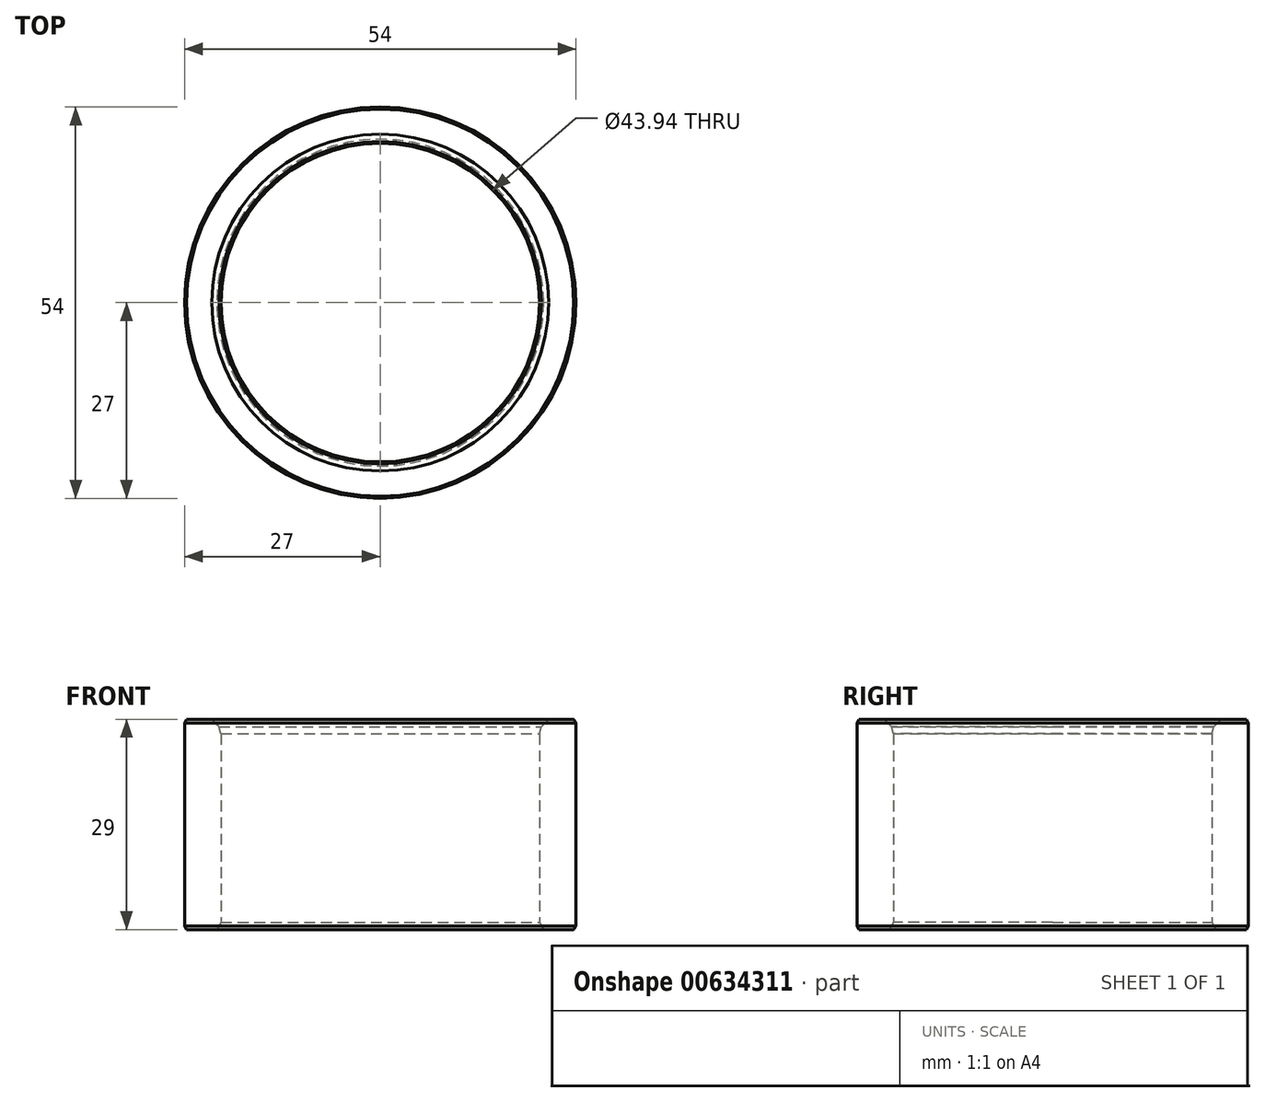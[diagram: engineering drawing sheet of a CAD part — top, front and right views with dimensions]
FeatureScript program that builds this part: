
annotation { "Feature Type Name" : "Feature", "Feature Type Description" : "" }
export const myFeature = defineFeature(function(context is Context, id is Id, definition is map)
    precondition{}
    {
        {
            var Q0;
            Q0=qCreatedBy(makeId("Top.planeOp"),FACE);
            var sketch = newSketch(context, id + "F0", { "sketchPlane" : qUnion([Q0])});
            skCircle(sketch, "E0", {"center": v(0, 0) * mm, "radius": 21.97 * mm});
            skCircle(sketch, "E1", {"center": v(0, 0) * mm, "radius": 27 * mm});
            skSolve(sketch);
        }
        {
            var Q0;
            Q0=makeQuery(id+"F0.imprint","IMPRINT",FACE,{"disambiguationData":[TD([[makeQuery(id+"F0.imprint","IMPRINT",EDGE,{"derivedFrom":sQuery(id+"F0.wireOp",EDGE,"E0")}),-1.0]])]});
            extrude(context, id + "F1", {"entities" : qUnion([Q0]), "depth" : 29 * mm, "offsetDistance" : 25 * mm});
        }
        {
            var Q0;
            Q0=makeQuery(id+"F1.opExtrude","CAP_EDGE",EDGE,{"disambiguationData":[OSD([sQuery(id+"F0.wireOp",EDGE,"E1")])],"isStart":false});
            var Q1;
            Q1=makeQuery(id+"F1.opExtrude","CAP_EDGE",EDGE,{"disambiguationData":[OSD([sQuery(id+"F0.wireOp",EDGE,"E1")])],"isStart":true});
            chamfer(context, id + "F2", {"entities" : qUnion([Q0, Q1]), "chamferType" : ChamferType.OFFSET_ANGLE, "width" : 0.5 * mm, "oppositeDirection" : true, "angle" : 30 * degree, "tangentPropagation" : true});
        }
        {
            var Q0;
            Q0=makeQuery(id+"F1.opExtrude","CAP_EDGE",EDGE,{"disambiguationData":[OSD([sQuery(id+"F0.wireOp",EDGE,"E0")])],"isStart":true});
            chamfer(context, id + "F3", {"entities" : qUnion([Q0]), "chamferType" : ChamferType.OFFSET_ANGLE, "width" : 1 * mm, "oppositeDirection" : true, "angle" : 30 * degree, "tangentPropagation" : true});
        }
        {
            var Q0;
            Q0=qCreatedBy(makeId("Front.planeOp"),FACE);
            var sketch = newSketch(context, id + "F4", { "sketchPlane" : qUnion([Q0])});
            skLineSegment(sketch, "E2", {"start": v(-21.97, 0) * mm, "end": v(-21.97, 29) * mm, "construction": true});
            skLineSegment(sketch, "E3", {"start": v(21.97, 29) * mm, "end": v(21.97, 0) * mm, "construction": true});
            skLineSegment(sketch, "E4.0.0", {"start": v(-26.71, 29) * mm, "end": v(26.71, 29) * mm, "construction": true});
            skLineSegment(sketch, "E5", {"start": v(-20.35, 28) * mm, "end": v(-23.75, 28) * mm, "construction": true});
            skLineSegment(sketch, "E6", {"start": v(-20.35, 27) * mm, "end": v(-23.75, 27) * mm, "construction": true});
            skLineSegment(sketch, "E7", {"start": v(-21.97, 27) * mm, "end": v(-22.24, 28) * mm});
            skLineSegment(sketch, "E8", {"start": v(-22.24, 28) * mm, "end": v(-23.24, 29) * mm});
            skLineSegment(sketch, "E9", {"start": v(-23.24, 29) * mm, "end": v(-21.97, 29) * mm});
            skLineSegment(sketch, "E10", {"start": v(-21.97, 27) * mm, "end": v(-21.97, 29) * mm});
            skLineSegment(sketch, "E11", {"start": v(0, 32.86) * mm, "end": v(0, -2.86) * mm, "construction": true});
            skPoint(sketch, "E11.startSnap0", {"position": v(0, 29) * mm});
            skSolve(sketch);
        }
        {
            var Q0;
            Q0=makeQuery(id+"F4.imprint","IMPRINT",FACE,{"disambiguationData":[TD([[makeQuery(id+"F4.imprint","IMPRINT",EDGE,{"derivedFrom":sQuery(id+"F4.wireOp",EDGE,"E7")}),-1.0]])]});
            var Q1;
            Q1=sQuery(id+"F4.wireOp",EDGE,"E11");
            revolve(context, id + "F5", {"operationType" : NewBodyOperationType.REMOVE, "entities" : qUnion([Q0]), "axis" : qUnion([Q1]), "revolveType" : RevolveType.FULL, "oppositeDirection" : true});
        }
    });
